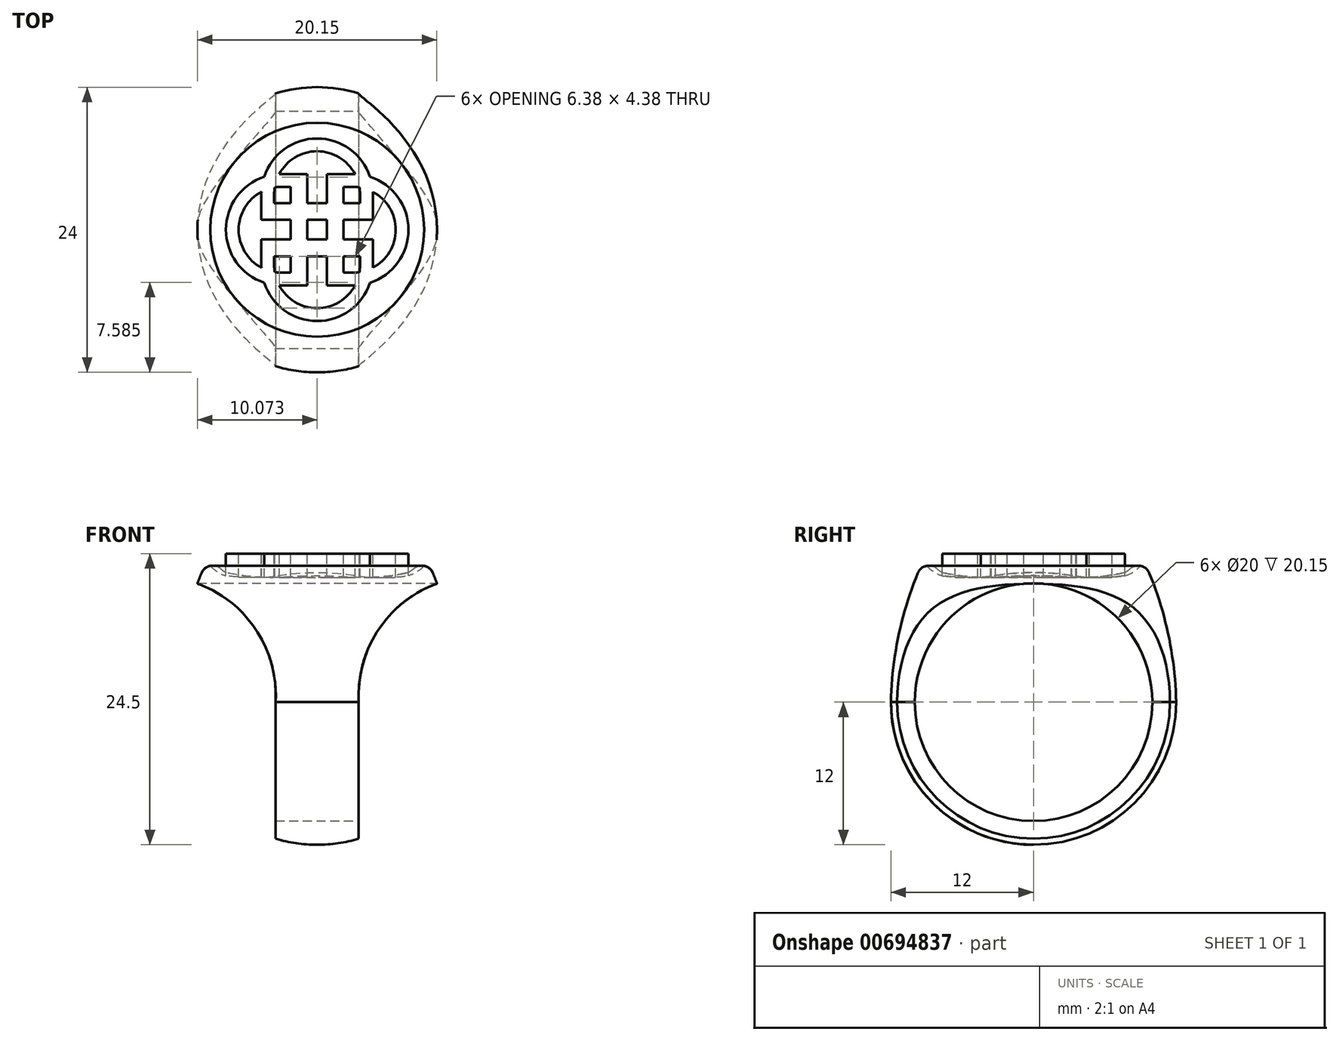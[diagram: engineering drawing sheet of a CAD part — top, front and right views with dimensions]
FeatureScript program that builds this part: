
annotation { "Feature Type Name" : "Feature", "Feature Type Description" : "" }
export const myFeature = defineFeature(function(context is Context, id is Id, definition is map)
    precondition{}
    {
        {
            var Q0;
            Q0=qCreatedBy(makeId("Right.planeOp"),FACE);
            var sketch = newSketch(context, id + "F0", { "sketchPlane" : qUnion([Q0])});
            skLineSegment(sketch, "E0", {"start": v(0, 0) * mm, "end": v(0, -24.5) * mm});
            skLineSegment(sketch, "E1", {"start": v(0, 0) * mm, "end": v(-9, 0) * mm});
            skArc(sketch, "E2", {"start": v(-12, -12.5) * mm, "mid": v(-8.49, -20.99) * mm, "end": v(0, -24.5) * mm});
            skLineSegment(sketch, "E3", {"start": v(0, -12.5) * mm, "end": v(-12, -12.5) * mm, "construction": true});
            skArc(sketch, "E4", {"start": v(-9, 0) * mm, "mid": v(-11.18, -6.09) * mm, "end": v(-12, -12.5) * mm});
            skSolve(sketch);
        }
        {
            var Q0;
            Q0=makeQuery(id+"F0.imprint","IMPRINT",FACE,{"disambiguationData":[TD([[makeQuery(id+"F0.imprint","IMPRINT",EDGE,{"derivedFrom":sQuery(id+"F0.wireOp",EDGE,"E0")}),-1.0]])]});
            var Q1;
            Q1=sQuery(id+"F0.wireOp",EDGE,"E0");
            revolve(context, id + "F1", {"entities" : qUnion([Q0]), "axis" : qUnion([Q1]), "revolveType" : RevolveType.FULL});
        }
        {
            var Q0;
            Q0=qCreatedBy(makeId("Right.planeOp"),FACE);
            var sketch = newSketch(context, id + "F2", { "sketchPlane" : qUnion([Q0])});
            skCircle(sketch, "E5", {"center": v(0, -12.5) * mm, "radius": 10 * mm});
            skSolve(sketch);
        }
        {
            var Q0;
            Q0=qSketchRegion(id+"F2",true);
            extrude(context, id + "F3", {"entities" : qUnion([Q0]), "operationType" : NewBodyOperationType.REMOVE, "endBound" : BoundingType.SYMMETRIC, "oppositeDirection" : true, "depth" : 25 * mm, "offsetDistance" : 25 * mm});
        }
        {
            var Q0;
            Q0=qCreatedBy(makeId("Front.planeOp"),FACE);
            var sketch = newSketch(context, id + "F4", { "sketchPlane" : qUnion([Q0])});
            skLineSegment(sketch, "E6", {"start": v(3.5, -26.5) * mm, "end": v(3.5, -12.5) * mm});
            skArc(sketch, "E7", {"start": v(10.15, -2.5) * mm, "mid": v(5.16, -6.39) * mm, "end": v(3.5, -12.5) * mm});
            skLineSegment(sketch, "E8", {"start": v(10.15, -2.5) * mm, "end": v(11.65, -2.5) * mm});
            skLineSegment(sketch, "E9", {"start": v(11.65, -2.5) * mm, "end": v(11.65, -26.5) * mm});
            skLineSegment(sketch, "E10", {"start": v(11.65, -26.5) * mm, "end": v(3.5, -26.5) * mm});
            skPoint(sketch, "E11.start.orphan", {"position": v(0, -24.5) * mm});
            skLineSegment(sketch, "E12", {"start": v(0, 0) * mm, "end": v(0, -24.5) * mm, "construction": true});
            skLineSegment(sketch, "E13.MirrorCS", {"start": v(-3.5, -26.5) * mm, "end": v(-3.5, -12.5) * mm});
            skArc(sketch, "E14.MirrorCS", {"start": v(-10.15, -2.5) * mm, "mid": v(-5.16, -6.39) * mm, "end": v(-3.5, -12.5) * mm});
            skLineSegment(sketch, "E15.MirrorCS", {"start": v(-11.65, -2.5) * mm, "end": v(-11.65, -26.5) * mm});
            skLineSegment(sketch, "E16.MirrorCS", {"start": v(-11.65, -26.5) * mm, "end": v(-3.5, -26.5) * mm});
            skLineSegment(sketch, "E17.MirrorCS", {"start": v(-10.15, -2.5) * mm, "end": v(-11.65, -2.5) * mm});
            skSolve(sketch);
        }
        {
            var Q0;
            Q0=qSketchRegion(id+"F4",true);
            extrude(context, id + "F5", {"entities" : qUnion([Q0]), "operationType" : NewBodyOperationType.REMOVE, "endBound" : BoundingType.SYMMETRIC, "depth" : 25 * mm, "offsetDistance" : 25 * mm});
        }
        {
            var Q0;
            Q0=makeQuery(id+"F1.opRevolve","SWEPT_FACE",FACE,{"disambiguationData":[OSD([sQuery(id+"F0.wireOp",EDGE,"E1")])]});
            var sketch = newSketch(context, id + "F6", { "sketchPlane" : qUnion([Q0])});
            skLineSegment(sketch, "E18", {"start": v(0, 22.3) * mm, "end": v(0, -22.61) * mm, "construction": true});
            skLineSegment(sketch, "E19", {"start": v(-20.58, 0) * mm, "end": v(20.94, 0) * mm, "construction": true});
            skPoint(sketch, "E20", {"position": v(-3, 0) * mm});
            skPoint(sketch, "E21", {"position": v(0, 0) * mm});
            skArc(sketch, "E22", {"start": v(-3, 4.69) * mm, "mid": v(-7.68, 0) * mm, "end": v(-3, -4.69) * mm});
            skArc(sketch, "E23", {"start": v(-3, 3.6) * mm, "mid": v(-6.6, 0) * mm, "end": v(-3, -3.6) * mm});
            skLineSegment(sketch, "E24", {"start": v(-3, 5.43) * mm, "end": v(-3, -5.16) * mm, "construction": true});
            skLineSegment(sketch, "E25", {"start": v(-3, 4.69) * mm, "end": v(-0.82, 4.69) * mm});
            skLineSegment(sketch, "E26", {"start": v(-0.82, 4.69) * mm, "end": v(-0.82, -4.69) * mm});
            skLineSegment(sketch, "E27", {"start": v(-0.82, -4.69) * mm, "end": v(-3, -4.69) * mm});
            skLineSegment(sketch, "E28", {"start": v(-3, 3.6) * mm, "end": v(-2.22, 3.6) * mm});
            skLineSegment(sketch, "E29", {"start": v(-2.22, 3.6) * mm, "end": v(-2.22, -3.6) * mm});
            skLineSegment(sketch, "E30", {"start": v(-2.22, -3.6) * mm, "end": v(-3, -3.61) * mm});
            skPoint(sketch, "E31", {"position": v(0, 3) * mm});
            skArc(sketch, "E32", {"start": v(4.68, 3) * mm, "mid": v(0, 7.68) * mm, "end": v(-4.7, 3) * mm});
            skArc(sketch, "E33", {"start": v(3.6, 3) * mm, "mid": v(0, 6.6) * mm, "end": v(-3.62, 3) * mm});
            skLineSegment(sketch, "E34", {"start": v(4.68, 3) * mm, "end": v(4.68, 0.83) * mm});
            skLineSegment(sketch, "E35", {"start": v(4.68, 0.83) * mm, "end": v(-4.7, 0.82) * mm});
            skLineSegment(sketch, "E36", {"start": v(-4.7, 0.82) * mm, "end": v(-4.7, 3) * mm});
            skLineSegment(sketch, "E37", {"start": v(3.6, 3) * mm, "end": v(3.6, 2.23) * mm});
            skLineSegment(sketch, "E38", {"start": v(3.6, 2.23) * mm, "end": v(-3.62, 2.22) * mm});
            skLineSegment(sketch, "E39", {"start": v(-3.62, 2.22) * mm, "end": v(-3.62, 3) * mm});
            skLineSegment(sketch, "E40.MirrorCS", {"start": v(0.82, 4.69) * mm, "end": v(0.82, -4.69) * mm});
            skLineSegment(sketch, "E41.MirrorCS", {"start": v(0.82, -4.69) * mm, "end": v(3, -4.69) * mm});
            skArc(sketch, "E42.MirrorCS", {"start": v(3, 4.69) * mm, "mid": v(7.68, 0) * mm, "end": v(3, -4.69) * mm});
            skLineSegment(sketch, "E43.MirrorCS", {"start": v(2.22, -3.6) * mm, "end": v(3, -3.61) * mm});
            skArc(sketch, "E44.MirrorCS", {"start": v(3, 3.6) * mm, "mid": v(6.6, 0) * mm, "end": v(3, -3.6) * mm});
            skLineSegment(sketch, "E45.MirrorCS", {"start": v(2.22, 3.6) * mm, "end": v(2.22, -3.6) * mm});
            skLineSegment(sketch, "E46.MirrorCS", {"start": v(3, 3.6) * mm, "end": v(2.22, 3.6) * mm});
            skLineSegment(sketch, "E47.MirrorCS", {"start": v(3, 4.69) * mm, "end": v(0.82, 4.69) * mm});
            skLineSegment(sketch, "E48.MirrorCS", {"start": v(4.68, -0.83) * mm, "end": v(-4.7, -0.82) * mm});
            skLineSegment(sketch, "E49.MirrorCS", {"start": v(3.6, -2.23) * mm, "end": v(-3.62, -2.22) * mm});
            skLineSegment(sketch, "E50.MirrorCS", {"start": v(-4.7, -0.82) * mm, "end": v(-4.7, -3) * mm});
            skArc(sketch, "E51.MirrorCS", {"start": v(4.68, -3) * mm, "mid": v(0, -7.68) * mm, "end": v(-4.7, -3) * mm});
            skArc(sketch, "E52.MirrorCS", {"start": v(3.6, -3) * mm, "mid": v(0, -6.6) * mm, "end": v(-3.62, -3) * mm});
            skLineSegment(sketch, "E53.MirrorCS", {"start": v(-3.62, -2.22) * mm, "end": v(-3.62, -3) * mm});
            skLineSegment(sketch, "E54.MirrorCS", {"start": v(3.6, -3) * mm, "end": v(3.6, -2.23) * mm});
            skLineSegment(sketch, "E55.MirrorCS", {"start": v(4.68, -3) * mm, "end": v(4.68, -0.83) * mm});
            skSolve(sketch);
        }
        {
            var Q0;
            {var subQ0=sQuery(id+"F6.wireOp",EDGE,"E36");Q0=makeQuery(id+"F6.imprint","IMPRINT",FACE,{"disambiguationData":[TD([[makeQuery(id+"F6.imprint","IMPRINT",EDGE,{"derivedFrom":subQ0}),1.0]])]});}
            var Q1;
            {var subQ6=sQuery(id+"F6.wireOp",EDGE,"E25");Q1=makeQuery(id+"F6.imprint","IMPRINT",FACE,{"disambiguationData":[TD([[makeQuery(id+"F6.imprint","IMPRINT",EDGE,{"derivedFrom":subQ6}),1.0]])]});}
            var Q2;
            {var subQ7=sQuery(id+"F6.wireOp",EDGE,"E34");Q2=makeQuery(id+"F6.imprint","IMPRINT",FACE,{"disambiguationData":[TD([[makeQuery(id+"F6.imprint","IMPRINT",EDGE,{"derivedFrom":subQ7}),1.0]])]});}
            var Q3;
            {var subQ9=sQuery(id+"F6.wireOp",EDGE,"E27");Q3=makeQuery(id+"F6.imprint","IMPRINT",FACE,{"disambiguationData":[TD([[makeQuery(id+"F6.imprint","IMPRINT",EDGE,{"derivedFrom":subQ9}),1.0]])]});}
            var Q4;
            Q4=makeQuery(id+"F6.imprint","IMPRINT",FACE,{"disambiguationData":[TD([[makeQuery(id+"F6.imprint","IMPRINT",EDGE,{"derivedFrom":makeQuery(id+"F1.opRevolve","SWEPT_EDGE",EDGE,{"disambiguationData":[OSD([sQuery(id+"F0.wireOp",EDGE,"E1"),sQuery(id+"F0.wireOp",EDGE,"E4")])]})}),1.0]])]});
            var Q5;
            {var subQ5=sQuery(id+"F6.wireOp",EDGE,"E28");Q5=makeQuery(id+"F6.imprint","IMPRINT",FACE,{"disambiguationData":[TD([[makeQuery(id+"F6.imprint","IMPRINT",EDGE,{"derivedFrom":subQ5}),-1.0]])]});}
            var Q6;
            {var subQ5=sQuery(id+"F6.wireOp",EDGE,"E37");Q6=makeQuery(id+"F6.imprint","IMPRINT",FACE,{"disambiguationData":[TD([[makeQuery(id+"F6.imprint","IMPRINT",EDGE,{"derivedFrom":subQ5}),-1.0]])]});}
            var Q7;
            {var subQ0=sQuery(id+"F6.wireOp",EDGE,"E30");Q7=makeQuery(id+"F6.imprint","IMPRINT",FACE,{"disambiguationData":[TD([[makeQuery(id+"F6.imprint","IMPRINT",EDGE,{"derivedFrom":subQ0}),-1.0]])]});}
            var Q8;
            {var subQ5=sQuery(id+"F6.wireOp",EDGE,"E43.MirrorCS");Q8=makeQuery(id+"F6.imprint","IMPRINT",FACE,{"disambiguationData":[TD([[makeQuery(id+"F6.imprint","IMPRINT",EDGE,{"derivedFrom":subQ5}),1.0]])]});}
            var Q9;
            {var subQ0=sQuery(id+"F6.wireOp",EDGE,"E35");var subQ1=sQuery(id+"F6.wireOp",EDGE,"E26");var subQ2=makeQuery(id+"F6.imprint","INTERSECT",VERTEX,{"derivedFrom":[subQ1,subQ0]});Q9=makeQuery(id+"F6.imprint","IMPRINT",FACE,{"disambiguationData":[TD([[makeQuery(id+"F6.imprint","IMPRINT",EDGE,{"disambiguationData":[TD([[subQ2,-1.0]])],"derivedFrom":subQ1}),1.0]])]});}
            extrude(context, id + "F7", {"entities" : qUnion([Q0, Q1, Q2, Q3, Q4, Q5, Q6, Q7, Q8, Q9]), "operationType" : NewBodyOperationType.REMOVE, "oppositeDirection" : true, "depth" : 2 * mm, "offsetDistance" : 25 * mm});
        }
        {
            var Q0;
            Q0=makeQuery(id+"F7.boolean.opBoolean","COPY",EDGE,{"derivedFrom":makeQuery(id+"F7.opExtrude","CAP_EDGE",EDGE,{"disambiguationData":[OSD([sQuery(id+"F0.wireOp",EDGE,"E1"),sQuery(id+"F0.wireOp",EDGE,"E4")])],"isStart":false})});
            fillet(context, id + "F8", {"entities" : qUnion([Q0]), "radius" : 3 * mm, "tangentPropagation" : true, "allowEdgeOverflow" : false});
        }
        {
            var Q0;
            {var subQ0=sQuery(id+"F0.wireOp",EDGE,"E4");Q0=makeQuery(id+"F8.opFillet","BLEND_EDGE",EDGE,{"blendedFrom":[makeQuery(id+"F7.boolean.opBoolean","COPY",EDGE,{"derivedFrom":makeQuery(id+"F7.opExtrude","CAP_EDGE",EDGE,{"disambiguationData":[OSD([sQuery(id+"F0.wireOp",EDGE,"E1"),subQ0])],"isStart":false})}),makeQuery(id+"F1.opRevolve","SWEPT_FACE",FACE,{"disambiguationData":[OSD([subQ0])]})],"blendedInto":[makeQuery(id+"F1.opRevolve","SWEPT_FACE",FACE,{"disambiguationData":[OSD([subQ0])]})]});}
            fillet(context, id + "F9", {"entities" : qUnion([Q0]), "radius" : 1 * mm, "tangentPropagation" : true, "allowEdgeOverflow" : false});
        }
    });
